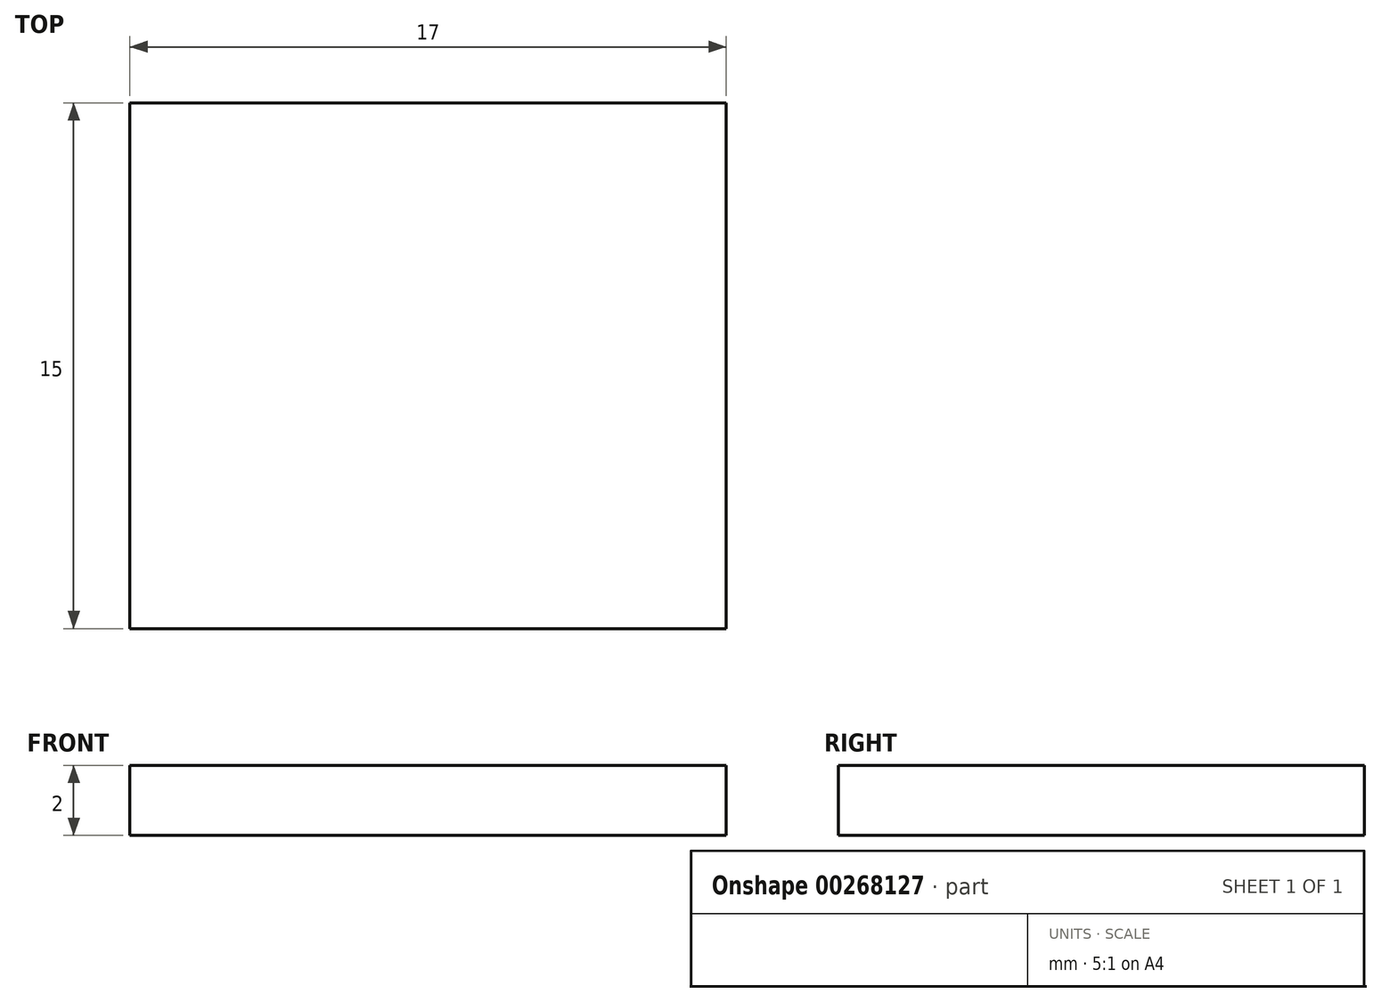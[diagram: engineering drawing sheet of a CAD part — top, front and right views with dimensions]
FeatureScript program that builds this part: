
annotation { "Feature Type Name" : "Feature", "Feature Type Description" : "" }
export const myFeature = defineFeature(function(context is Context, id is Id, definition is map)
    precondition{}
    {
        {
            var Q0;
            Q0=qCreatedBy(makeId("Top.planeOp"),FACE);
            var sketch = newSketch(context, id + "F0", { "sketchPlane" : qUnion([Q0])});
            skLineSegment(sketch, "E0.bottom", {"start": v(-8.5, 7.5) * mm, "end": v(8.5, 7.5) * mm});
            skLineSegment(sketch, "E0.top", {"start": v(-8.5, -7.5) * mm, "end": v(8.5, -7.5) * mm});
            skLineSegment(sketch, "E0.left", {"start": v(-8.5, 7.5) * mm, "end": v(-8.5, -7.5) * mm});
            skLineSegment(sketch, "E0.right", {"start": v(8.5, 7.5) * mm, "end": v(8.5, -7.5) * mm});
            skPoint(sketch, "E0.middle", {"position": v(0, 0) * mm});
            skSolve(sketch);
        }
        {
            var Q0;
            Q0=makeQuery(id+"F0.imprint","IMPRINT",FACE,{"disambiguationData":[TD([[makeQuery(id+"F0.imprint","IMPRINT",EDGE,{"derivedFrom":sQuery(id+"F0.wireOp",EDGE,"E0.bottom")}),-1.0]])]});
            extrude(context, id + "F1", {"entities" : qUnion([Q0]), "depth" : 2 * mm, "offsetDistance" : 25 * mm});
        }
    });
